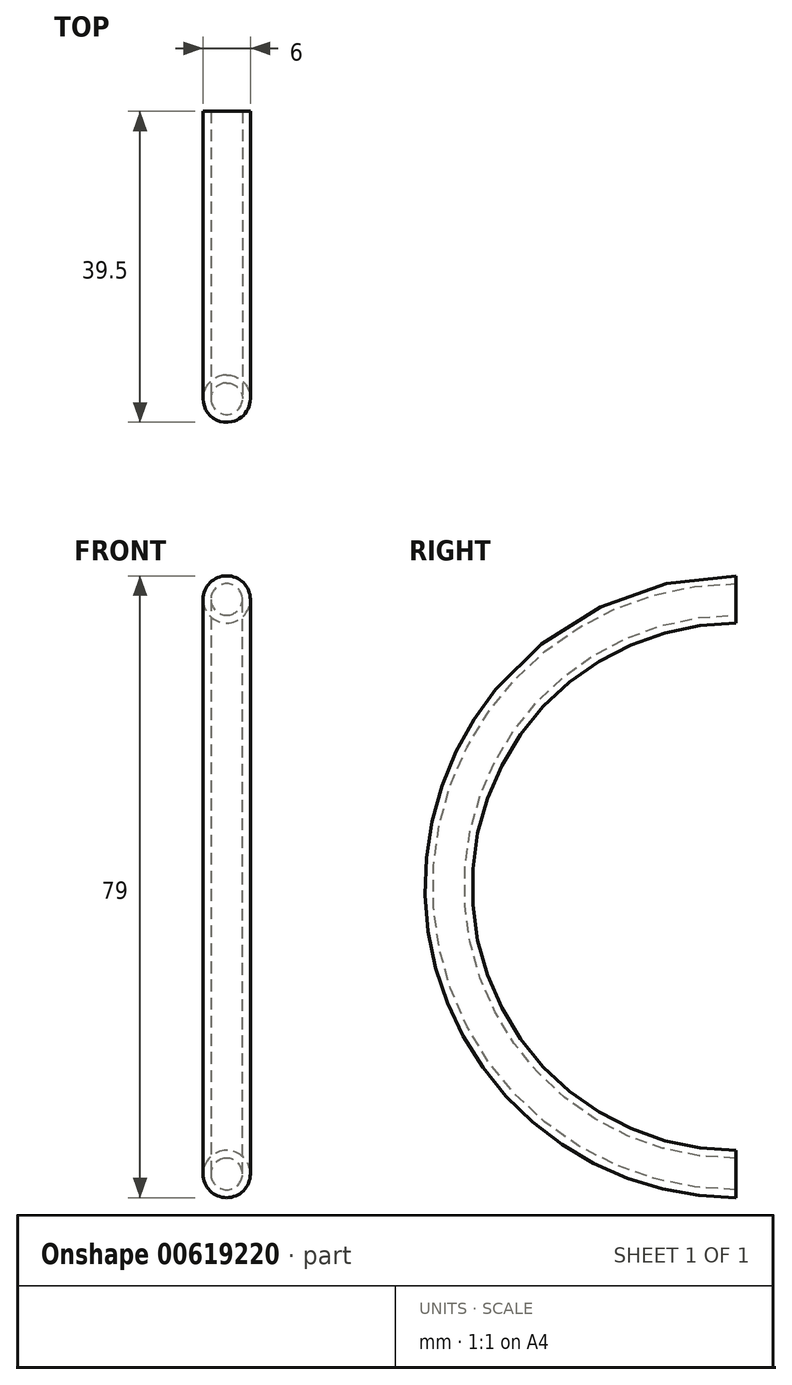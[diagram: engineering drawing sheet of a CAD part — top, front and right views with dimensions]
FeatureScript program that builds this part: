
annotation { "Feature Type Name" : "Feature", "Feature Type Description" : "" }
export const myFeature = defineFeature(function(context is Context, id is Id, definition is map)
    precondition{}
    {
        {
            var Q0;
            Q0=qCreatedBy(makeId("Front.planeOp"),FACE);
            var sketch = newSketch(context, id + "F0", { "sketchPlane" : qUnion([Q0])});
            skLineSegment(sketch, "E0", {"start": v(-56.83, 36.5) * mm, "end": v(64.46, 36.5) * mm, "construction": true});
            skLineSegment(sketch, "E1", {"start": v(-55.58, -36.5) * mm, "end": v(56.46, -36.5) * mm, "construction": true});
            skLineSegment(sketch, "E2", {"start": v(0, 45.46) * mm, "end": v(0, -39.6) * mm, "construction": true});
            skLineSegment(sketch, "E3", {"start": v(-55.29, 0) * mm, "end": v(61.15, 0) * mm, "construction": true});
            skCircle(sketch, "E4", {"center": v(0, 36.5) * mm, "radius": 3 * mm});
            skCircle(sketch, "E5", {"center": v(0, 36.5) * mm, "radius": 2 * mm});
            skSolve(sketch);
        }
        {
            var Q0;
            Q0=makeQuery(id+"F0.imprint","IMPRINT",FACE,{"disambiguationData":[TD([[makeQuery(id+"F0.imprint","IMPRINT",EDGE,{"derivedFrom":sQuery(id+"F0.wireOp",EDGE,"E4")}),1.0]])]});
            var Q1;
            Q1=sQuery(id+"F0.wireOp",EDGE,"E4");
            var Q2;
            Q2=sQuery(id+"F0.wireOp",EDGE,"E5");
            var Q3;
            Q3=sQuery(id+"F0.wireOp",EDGE,"E3");
            revolve(context, id + "F1", {"entities" : qUnion([Q0]), "surfaceEntities" : qUnion([Q1, Q2]), "axis" : qUnion([Q3]), "revolveType" : RevolveType.ONE_DIRECTION, "angle" : 180 * degree});
        }
    });
